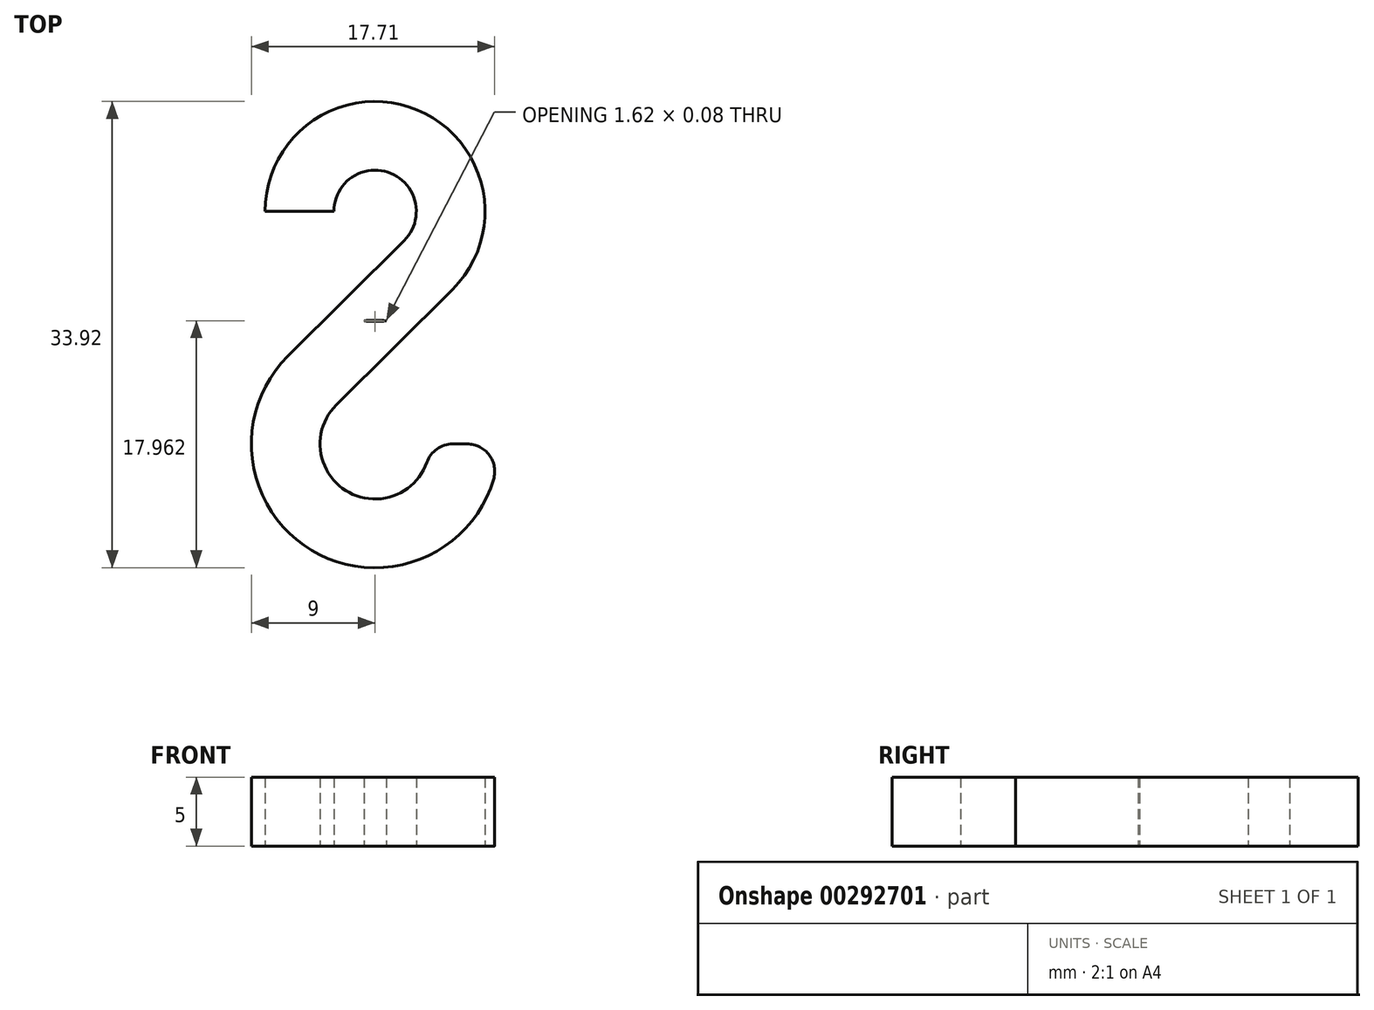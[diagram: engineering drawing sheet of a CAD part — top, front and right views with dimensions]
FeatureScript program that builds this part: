
annotation { "Feature Type Name" : "Feature", "Feature Type Description" : "" }
export const myFeature = defineFeature(function(context is Context, id is Id, definition is map)
    precondition{}
    {
        {
            var Q0;
            Q0=qCreatedBy(makeId("Top.planeOp"),FACE);
            var sketch = newSketch(context, id + "F0", { "sketchPlane" : qUnion([Q0])});
            skCircle(sketch, "E0", {"center": v(0, 5.67) * mm, "radius": 3 * mm});
            skCircle(sketch, "E1", {"center": v(0, -11.25) * mm, "radius": 4 * mm});
            skCircle(sketch, "E2.0", {"center": v(0, 5.67) * mm, "radius": 8 * mm});
            skCircle(sketch, "E3.0", {"center": v(0, -11.25) * mm, "radius": 9 * mm});
            skLineSegment(sketch, "E4", {"start": v(-3, 5.67) * mm, "end": v(-8, 5.67) * mm});
            skPoint(sketch, "E5", {"position": v(0, -2.25) * mm});
            skPoint(sketch, "E6", {"position": v(0, 2.67) * mm});
            skLineSegment(sketch, "E7", {"start": v(2.12, 3.55) * mm, "end": v(-6.35, -4.87) * mm});
            skLineSegment(sketch, "E8", {"start": v(-2.82, -8.41) * mm, "end": v(5.64, 0) * mm});
            skLineSegment(sketch, "E9", {"start": v(4, -11.25) * mm, "end": v(9, -11.25) * mm});
            skSolve(sketch);
        }
        {
            var Q0;
            {var subQ0=sQuery(id+"F0.wireOp",EDGE,"E4");Q0=makeQuery(id+"F0.imprint","IMPRINT",FACE,{"disambiguationData":[TD([[makeQuery(id+"F0.imprint","IMPRINT",EDGE,{"derivedFrom":subQ0}),-1.0]])]});}
            var Q1;
            {var subQ0=sQuery(id+"F0.wireOp",EDGE,"E7");var subQ1=sQuery(id+"F0.wireOp",EDGE,"E2.0");var subQ2=makeQuery(id+"F0.imprint","INTERSECT",VERTEX,{"derivedFrom":[subQ1,subQ0]});Q1=makeQuery(id+"F0.imprint","IMPRINT",FACE,{"disambiguationData":[TD([[makeQuery(id+"F0.imprint","IMPRINT",EDGE,{"disambiguationData":[TD([[subQ2,-1.0]])],"derivedFrom":subQ1}),-1.0]])]});}
            var Q2;
            {var subQ0=sQuery(id+"F0.wireOp",EDGE,"E8");var subQ1=sQuery(id+"F0.wireOp",EDGE,"E2.0");var subQ2=makeQuery(id+"F0.imprint","INTERSECT",VERTEX,{"derivedFrom":[subQ1,subQ0]});Q2=makeQuery(id+"F0.imprint","IMPRINT",FACE,{"disambiguationData":[TD([[makeQuery(id+"F0.imprint","IMPRINT",EDGE,{"disambiguationData":[TD([[subQ2,1.0]])],"derivedFrom":subQ1}),-1.0]])]});}
            var Q3;
            {var subQ9=sQuery(id+"F0.wireOp",EDGE,"E9");Q3=makeQuery(id+"F0.imprint","IMPRINT",FACE,{"disambiguationData":[TD([[makeQuery(id+"F0.imprint","IMPRINT",EDGE,{"derivedFrom":subQ9}),-1.0]])]});}
            extrude(context, id + "F1", {"entities" : qUnion([Q0, Q1, Q2, Q3]), "depth" : 5 * mm});
        }
        {
            var Q0;
            Q0=makeQuery(id+"F1.opExtrude","SWEPT_EDGE",EDGE,{"disambiguationData":[OSD([sQuery(id+"F0.wireOp",EDGE,"E1"),sQuery(id+"F0.wireOp",EDGE,"E9")])]});
            var Q1;
            Q1=makeQuery(id+"F1.opExtrude","SWEPT_EDGE",EDGE,{"disambiguationData":[OSD([sQuery(id+"F0.wireOp",EDGE,"E3.0"),sQuery(id+"F0.wireOp",EDGE,"E9")])]});
            fillet(context, id + "F2", {"entities" : qUnion([Q0, Q1]), "radius" : 2 * mm, "tangentPropagation" : true, "allowEdgeOverflow" : false});
        }
    });
